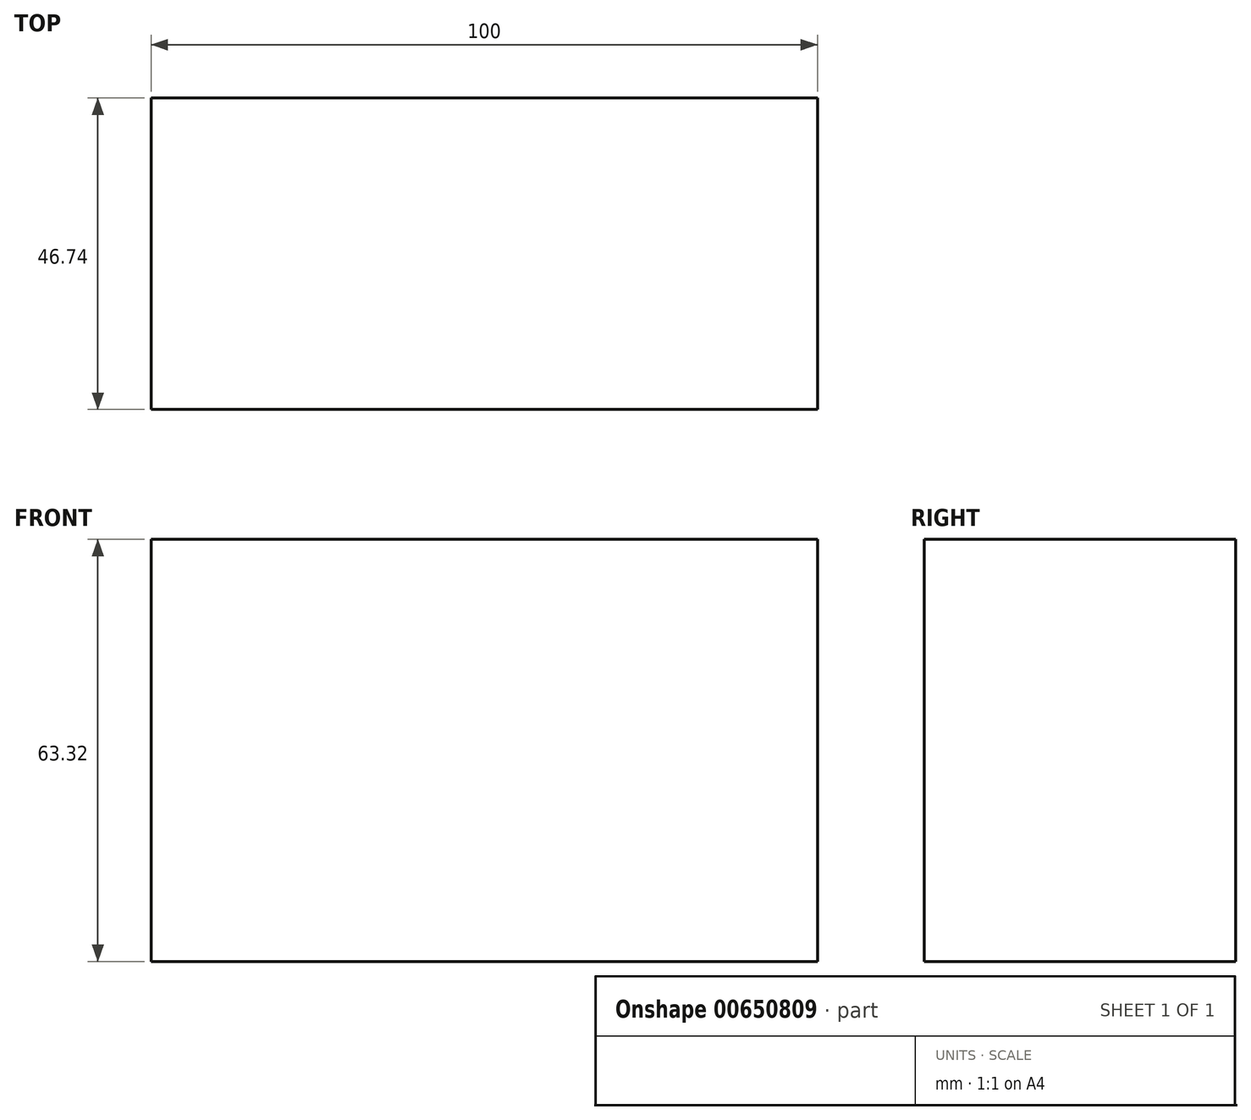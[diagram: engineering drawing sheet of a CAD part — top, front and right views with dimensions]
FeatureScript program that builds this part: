
annotation { "Feature Type Name" : "Feature", "Feature Type Description" : "" }
export const myFeature = defineFeature(function(context is Context, id is Id, definition is map)
    precondition{}
    {
        {
            var Q0;
            Q0=qCreatedBy(makeId("Front.planeOp"),FACE);
            var sketch = newSketch(context, id + "F0", { "sketchPlane" : qUnion([Q0])});
            skLineSegment(sketch, "E0.bottom", {"start": v(-57.33, 34.05) * mm, "end": v(42.67, 34.05) * mm});
            skLineSegment(sketch, "E0.top", {"start": v(-57.33, -29.27) * mm, "end": v(42.67, -29.27) * mm});
            skLineSegment(sketch, "E0.left", {"start": v(-57.33, 34.05) * mm, "end": v(-57.33, -29.27) * mm});
            skLineSegment(sketch, "E0.right", {"start": v(42.67, 34.05) * mm, "end": v(42.67, -29.27) * mm});
            skSolve(sketch);
        }
        {
            var Q0;
            Q0 = qSketchRegion(id + "F0", true);
            var Q1;
            Q1=makeQuery(id+"F0.imprint","IMPRINT",FACE,{"disambiguationData":[TD([[makeQuery(id+"F0.imprint","IMPRINT",EDGE,{"derivedFrom":sQuery(id+"F0.wireOp",EDGE,"E0.bottom")}),-1.0]])]});
            extrude(context, id + "F1", {"entities" : qUnion([Q0, Q1]), "depth" : 25.4 * mm, "offsetDistance" : 25.4 * mm});
        }
        {
            var Q0;
            Q0=makeQuery(id+"F1.opExtrude","CAP_FACE",FACE,{"disambiguationData":[OSD([sQuery(id+"F0.wireOp",EDGE,"E0.bottom"),sQuery(id+"F0.wireOp",EDGE,"E0.top"),sQuery(id+"F0.wireOp",EDGE,"E0.left"),sQuery(id+"F0.wireOp",EDGE,"E0.right")])],"isStart":false});
            extrude(context, id + "F2", {"entities" : qUnion([Q0]), "operationType" : NewBodyOperationType.ADD, "depth" : 21.34 * mm, "offsetDistance" : 25.4 * mm});
        }
    });
